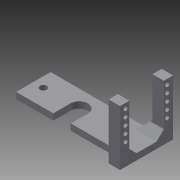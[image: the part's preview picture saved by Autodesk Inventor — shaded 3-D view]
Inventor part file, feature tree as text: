
AUTODESK INVENTOR PART (.ipt)
format: ipt  version: 2013 (Build 170138000, 138)  size: 169,984 bytes
history: native  units: mm
features: sketch x4, extrude x3, chamfer x3, hole x1
ambient origin geometry x8: Origin, YZ Plane, XZ Plane, XY Plane, X Axis, Y Axis, Z Axis, Center Point
bodies: Solid1 (feature_tree)
feature tree (11):
  extrude  "Extrusion1"  Depth=24.0mm
  extrude  "Extrusion2"  Depth=8.0mm
  chamfer  "Chamfer1"  Distance=38.6mm
  extrude  "Extrusion4"  Depth=6.5mm TaperAngle=45.0deg
  hole  "Hole2"  [1 undecoded]
  chamfer  "Chamfer2"  Distance=12.2mm
  chamfer  "Chamfer3"  Distance=50.0mm
  sketch  "Sketch1"  dims[d0=79.0mm d1=24.0mm]
  sketch  "Sketch3"  dims[d2=4.4mm d3=0.0mm d8=8.0mm]
  sketch  "Sketch5"  dims[d9=6.5mm]
  sketch  "Sketch6"  dims[d10=6.5mm d11=38.6mm d12=0.0mm d26=6.5mm d27=2.0mm d28=45.0deg d29=64.0mm d30=12.2mm d31=50.0mm d32=4.8mm d33=4.8mm d36=5.6mm d37=0.0mm d42=5.0mm d43=5.0mm d44=1.0mm d45=5.0mm d46=5.0mm d47=3.0mm d48=6.0mm d49=4.0mm d50=2.0mm d51=90.0deg d52=8.0mm d53=20.594885mm d54=33.0mm d55=1.0mm d56=6.4mm d57=2.0mm d58=45.0deg d59=5.0mm d60=5.0mm d61=5.0mm d62=5.0mm d63=5.0mm d64=2.0mm d65=45.0deg]
note: 1 required parameter value undecoded (feature->parameter linkage not recoverable at this tier; creation-order binding heuristic only, values carry confidence <= 0.55)
